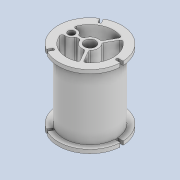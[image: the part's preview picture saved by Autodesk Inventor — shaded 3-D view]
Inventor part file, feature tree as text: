
AUTODESK INVENTOR PART (.ipt)
format: ipt  version: 2020 (Build 240168000, 168)  size: 406,016 bytes
history: native  units: mm
features: extrude x6, sketch x6, fillet x4, projected_geometry x4, pattern_circular x1
ambient origin geometry x8: Origin, YZ Plane, XZ Plane, XY Plane, X Axis, Y Axis, Z Axis, Center Point
bodies: Solid1 (feature_tree)
feature tree (21):
  extrude  "Extrusion1"  Depth=3.0mm
  extrude  "Extrusion2"  Depth=0.7mm
  extrude  "Extrusion3"  Depth=0.7mm
  extrude  "Extrusion4"  Depth=5.0mm
  extrude  "Extrusion5"  Depth=19.5mm TaperAngle=0.0deg
  pattern_circular  "Circular Pattern1"  [2 undecoded]
  fillet  "Fillet1"  Radius=1.5mm
  fillet  "Fillet2"  Radius=1.0mm
  extrude  "Extrusion6"  Depth=0.5mm TaperAngle=0.0deg
  fillet  "Fillet3"  [1 undecoded]
  fillet  "Fillet4"  Radius=3.0mm
  sketch  "Sketch1"  dims[d0=14.0mm d1=3.0mm]
  sketch  "Sketch2"  dims[d2=0.7mm d3=0.7mm]
  projected_geometry  "Projected Loop1"
  sketch  "Sketch3"  dims[d4=3.5mm d5=0.7mm]
  projected_geometry  "Projected Loop2"
  sketch  "Sketch4"  dims[d6=30.0mm d8=360.0deg d10=5.0mm]
  projected_geometry  "Projected Loop3"
  sketch  "Sketch5"  dims[d11=3.0mm d12=19.5mm d13=0.0mm]
  projected_geometry  "Projected Loop4"
  sketch  "Sketch6"  dims[d14=1.8mm d15=19.5mm d16=0.0mm d17=1.5mm d18=1.0mm d19=0.0mm d20=1.0mm d21=0.0mm d22=60.0deg d23=3.0mm d24=0.7mm d25=20.0mm d26=0.0mm d27=30.0mm d28=360.0deg d30=0.2mm d31=0.5mm d32=5.5mm d33=2.0mm d34=0.0mm d35=0.5mm d36=0.5mm]
note: 3 required parameter values undecoded (feature->parameter linkage not recoverable at this tier; creation-order binding heuristic only, values carry confidence <= 0.55)
